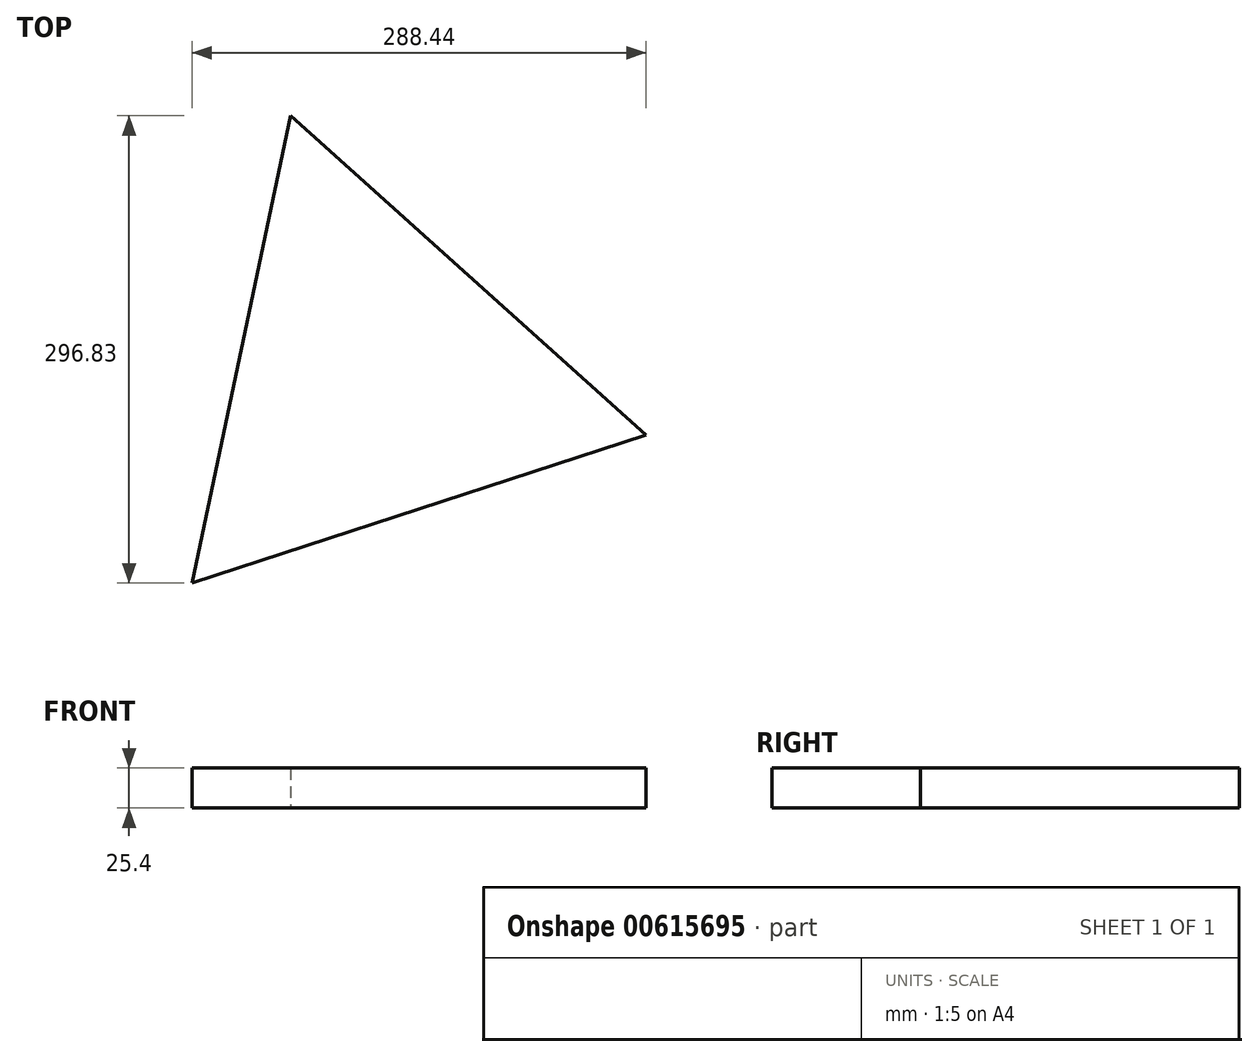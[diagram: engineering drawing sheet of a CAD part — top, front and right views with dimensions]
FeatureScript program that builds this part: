
annotation { "Feature Type Name" : "Feature", "Feature Type Description" : "" }
export const myFeature = defineFeature(function(context is Context, id is Id, definition is map)
    precondition{}
    {
        {
            var Q0;
            Q0=qCreatedBy(makeId("Top.planeOp"),FACE);
            var sketch = newSketch(context, id + "F0", { "sketchPlane" : qUnion([Q0])});
            skLineSegment(sketch, "E0.bottom", {"start": v(25.35, -20.51) * mm, "end": v(-71.46, -20.51) * mm});
            skLineSegment(sketch, "E0.top", {"start": v(25.35, 26.76) * mm, "end": v(-71.46, 26.76) * mm});
            skLineSegment(sketch, "E0.left", {"start": v(25.35, -20.51) * mm, "end": v(25.35, 26.76) * mm});
            skLineSegment(sketch, "E0.right", {"start": v(-71.46, -20.51) * mm, "end": v(-71.46, 26.76) * mm});
            skLineSegment(sketch, "E1.bottom", {"start": v(25.35, -11.38) * mm, "end": v(84.32, -11.38) * mm});
            skLineSegment(sketch, "E1.top", {"start": v(25.35, 23.44) * mm, "end": v(84.32, 23.44) * mm});
            skLineSegment(sketch, "E1.left", {"start": v(25.35, -11.38) * mm, "end": v(25.35, 23.44) * mm});
            skLineSegment(sketch, "E1.right", {"start": v(84.32, -11.38) * mm, "end": v(84.32, 23.44) * mm});
            skLineSegment(sketch, "E2.bottom", {"start": v(84.32, -11.38) * mm, "end": v(25.35, -11.38) * mm});
            skLineSegment(sketch, "E2.top", {"start": v(84.32, -20.51) * mm, "end": v(25.35, -20.51) * mm});
            skLineSegment(sketch, "E2.left", {"start": v(84.32, -11.38) * mm, "end": v(84.32, -20.51) * mm});
            skLineSegment(sketch, "E2.right", {"start": v(25.35, -11.38) * mm, "end": v(25.35, -20.51) * mm});
            skSolve(sketch);
        }
        {
            var Q0;
            Q0=makeQuery(id+"F0.imprint","IMPRINT",FACE,{"disambiguationData":[TD([[makeQuery(id+"F0.imprint","IMPRINT",EDGE,{"derivedFrom":sQuery(id+"F0.wireOp",EDGE,"E0.bottom")}),-1.0]])]});
            var sketch = newSketch(context, id + "F1", { "sketchPlane" : qUnion([Q0])});
            skCircle(sketch, "E3.cCircle", {"center": v(-27.15, 0) * mm, "radius": 87.58 * mm, "construction": true});
            skLineSegment(sketch, "E3.0", {"start": v(144.22, -36.23) * mm, "end": v(-144.22, -130.3) * mm});
            skLineSegment(sketch, "E3.1", {"start": v(-144.22, -130.3) * mm, "end": v(-81.46, 166.53) * mm});
            skLineSegment(sketch, "E3.2", {"start": v(-81.46, 166.53) * mm, "end": v(144.22, -36.23) * mm});
            skPoint(sketch, "E3.0.midPoint", {"position": v(0, -83.26) * mm});
            skSolve(sketch);
        }
        {
            var Q0;
            Q0=makeQuery(id+"F1.imprint","IMPRINT",FACE,{"disambiguationData":[TD([[makeQuery(id+"F1.imprint","IMPRINT",EDGE,{"derivedFrom":makeQuery(id+"F0.imprint","IMPRINT",EDGE,{"derivedFrom":sQuery(id+"F0.wireOp",EDGE,"E0.bottom")})}),-1.0]])]});
            var Q1;
            Q1=makeQuery(id+"F1.imprint","IMPRINT",FACE,{"disambiguationData":[TD([[makeQuery(id+"F1.imprint","IMPRINT",EDGE,{"derivedFrom":sQuery(id+"F1.wireOp",EDGE,"E3.0")}),-1.0]])]});
            extrude(context, id + "F2", {"entities" : qUnion([Q0, Q1]), "depth" : 25.4 * mm, "offsetDistance" : 25.4 * mm});
        }
        {
            var Q0;
            Q0=makeQuery(id+"F2.opExtrude","CAP_FACE",FACE,{"disambiguationData":[OSD([sQuery(id+"F1.wireOp",EDGE,"E3.0"),sQuery(id+"F1.wireOp",EDGE,"E3.1"),sQuery(id+"F1.wireOp",EDGE,"E3.2")])],"isStart":false});
            var sketch = newSketch(context, id + "F3", { "sketchPlane" : qUnion([Q0])});
            skCircle(sketch, "E4", {"center": v(-14.48, 47.62) * mm, "radius": 42.46 * mm});
            skSolve(sketch);
        }
    });
